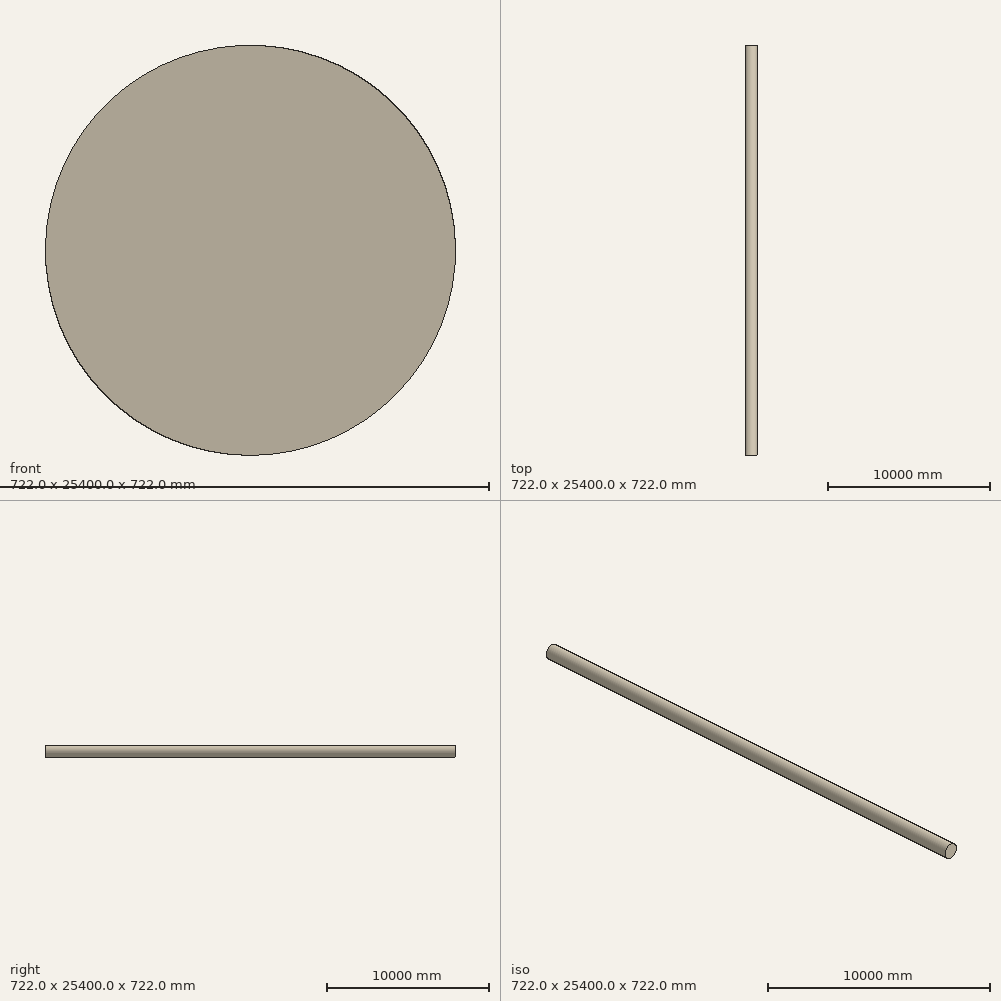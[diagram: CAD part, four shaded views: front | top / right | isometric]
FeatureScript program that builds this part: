
annotation { "Feature Type Name" : "Feature", "Feature Type Description" : "" }
export const myFeature = defineFeature(function(context is Context, id is Id, definition is map)
    precondition{}
    {
        {
            var Q0;
            Q0=qCreatedBy(makeId("Front.planeOp"),FACE);
            var sketch = newSketch(context, id + "F0", { "sketchPlane" : qUnion([Q0])});
            skCircle(sketch, "E0", {"center": v(0, 0) * mm, "radius": 361 * mm});
            skSolve(sketch);
        }
        {
            var Q0;
            Q0=makeQuery(id+"F0.imprint","IMPRINT",FACE,{"disambiguationData":[TD([[makeQuery(id+"F0.imprint","IMPRINT",EDGE,{"derivedFrom":sQuery(id+"F0.wireOp",EDGE,"E0")}),1.0]])]});
            extrude(context, id + "F1", {"entities" : qUnion([Q0]), "depth" : 25400 * mm, "offsetDistance" : 25.4 * mm});
        }
    });
